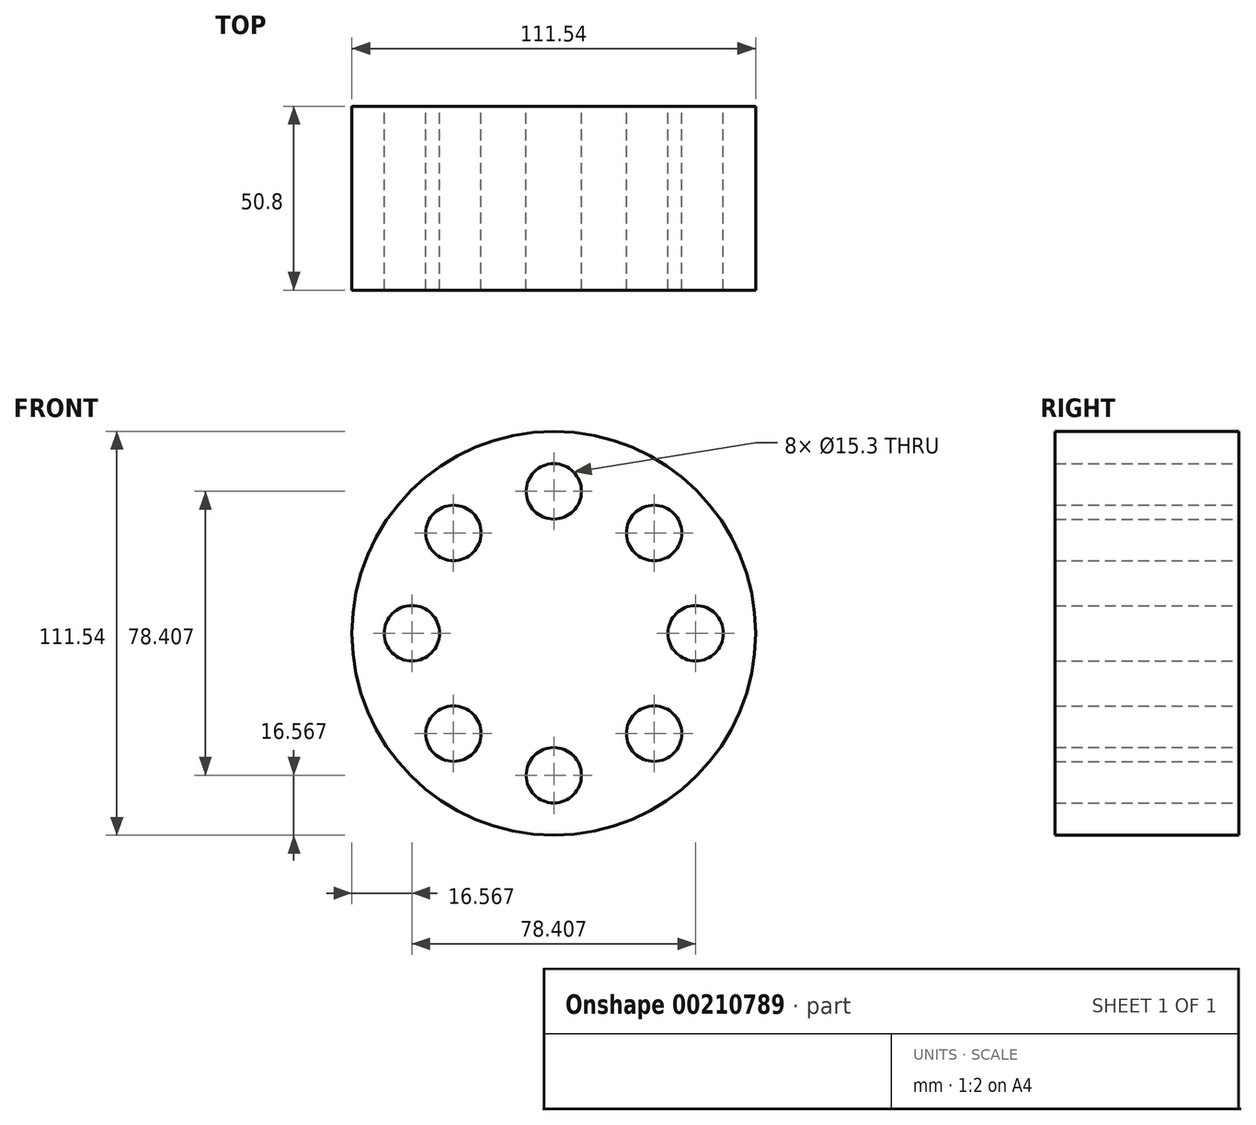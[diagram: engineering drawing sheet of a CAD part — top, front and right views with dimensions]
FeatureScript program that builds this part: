
annotation { "Feature Type Name" : "Feature", "Feature Type Description" : "" }
export const myFeature = defineFeature(function(context is Context, id is Id, definition is map)
    precondition{}
    {
        {
            var Q0;
            Q0=qCreatedBy(makeId("Front.planeOp"),FACE);
            var sketch = newSketch(context, id + "F0", { "sketchPlane" : qUnion([Q0])});
            skCircle(sketch, "E0", {"center": v(0, 0) * mm, "radius": 55.77 * mm});
            skSolve(sketch);
        }
        {
            var Q0;
            Q0=makeQuery(id+"F0.imprint","IMPRINT",FACE,{"disambiguationData":[TD([[makeQuery(id+"F0.imprint","IMPRINT",EDGE,{"derivedFrom":sQuery(id+"F0.wireOp",EDGE,"E0")}),1.0]])]});
            var sketch = newSketch(context, id + "F1", { "sketchPlane" : qUnion([Q0])});
            skCircle(sketch, "E1", {"center": v(0, 39.2) * mm, "radius": 7.65 * mm});
            skCircle(sketch, "E2.1.0", {"center": v(-27.72, 27.72) * mm, "radius": 7.65 * mm});
            skCircle(sketch, "E2.2.0", {"center": v(-39.2, 0) * mm, "radius": 7.65 * mm});
            skCircle(sketch, "E2.3.0", {"center": v(-27.72, -27.72) * mm, "radius": 7.65 * mm});
            skCircle(sketch, "E2.4.0", {"center": v(0, -39.2) * mm, "radius": 7.65 * mm});
            skCircle(sketch, "E2.5.0", {"center": v(27.72, -27.72) * mm, "radius": 7.65 * mm});
            skCircle(sketch, "E2.6.0", {"center": v(39.2, 0) * mm, "radius": 7.65 * mm});
            skCircle(sketch, "E2.7.0", {"center": v(27.72, 27.72) * mm, "radius": 7.65 * mm});
            skPoint(sketch, "E2.center", {"position": v(0, 0) * mm});
            skSolve(sketch);
        }
        {
            var Q0;
            Q0=makeQuery(id+"F1.imprint","IMPRINT",FACE,{"disambiguationData":[TD([[makeQuery(id+"F1.imprint","IMPRINT",EDGE,{"derivedFrom":sQuery(id+"F1.wireOp",EDGE,"E1")}),-1.0]])]});
            extrude(context, id + "F2", {"entities" : qUnion([Q0]), "depth" : 50.8 * mm});
        }
    });
